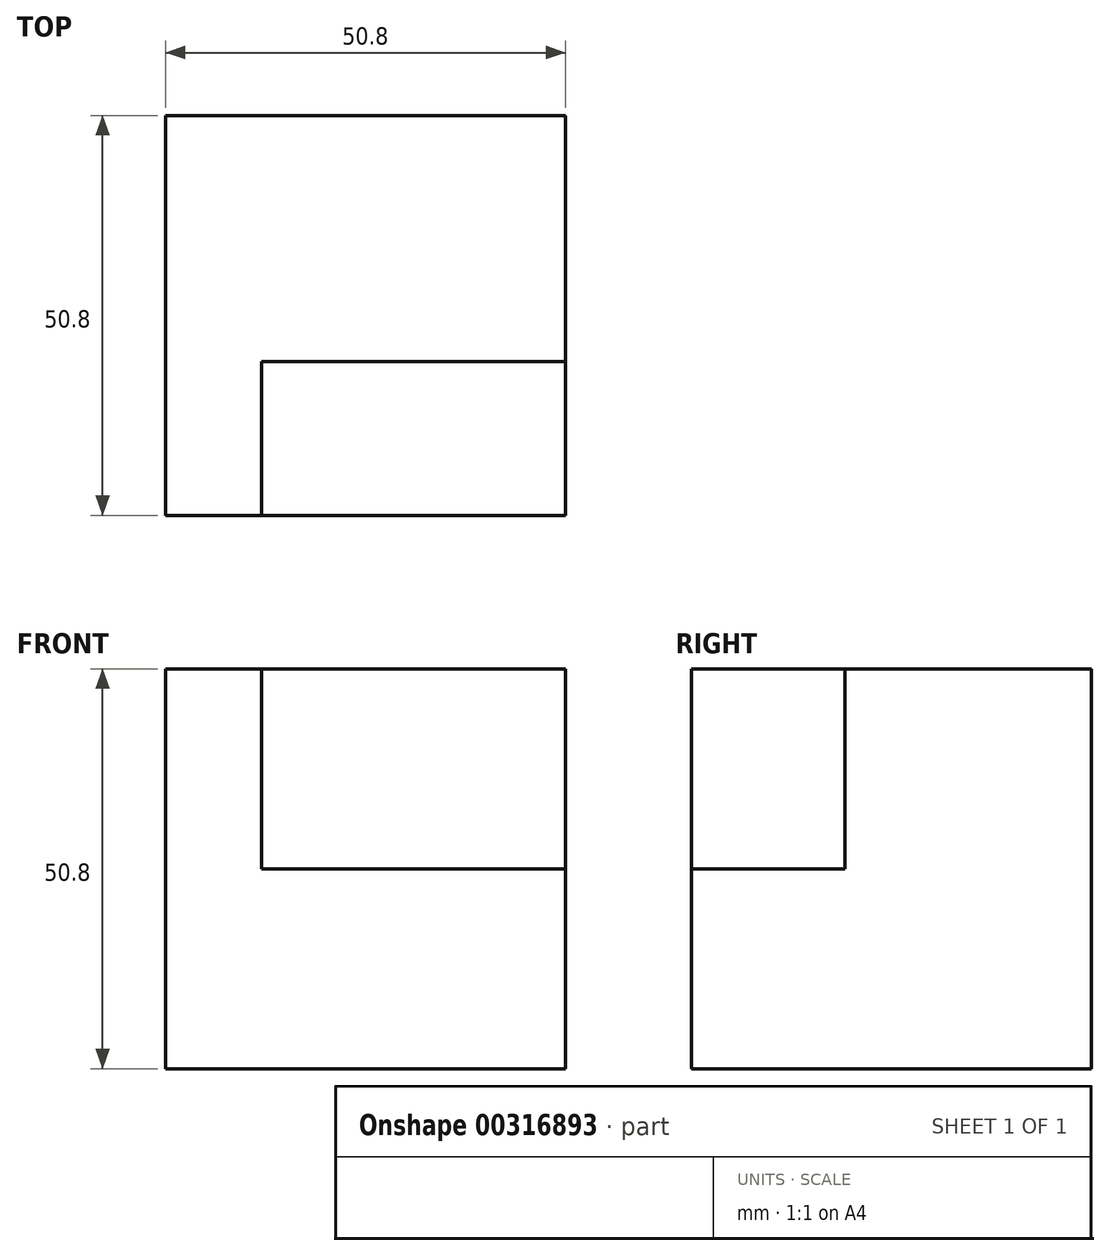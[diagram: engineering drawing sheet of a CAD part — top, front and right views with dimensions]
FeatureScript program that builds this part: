
annotation { "Feature Type Name" : "Feature", "Feature Type Description" : "" }
export const myFeature = defineFeature(function(context is Context, id is Id, definition is map)
    precondition{}
    {
        {
            var Q0;
            Q0=qCreatedBy(makeId("Top.planeOp"),FACE);
            var sketch = newSketch(context, id + "F0", { "sketchPlane" : qUnion([Q0])});
            skLineSegment(sketch, "E0", {"start": v(9.09, 37.8) * mm, "end": v(-41.71, 37.8) * mm});
            skLineSegment(sketch, "E1", {"start": v(-41.71, 37.8) * mm, "end": v(-41.71, -13) * mm});
            skLineSegment(sketch, "E2", {"start": v(-41.71, -13) * mm, "end": v(9.09, -13) * mm});
            skLineSegment(sketch, "E3", {"start": v(9.09, -13) * mm, "end": v(9.09, 37.8) * mm});
            skSolve(sketch);
        }
        {
            var Q0;
            Q0 = qSketchRegion(id + "F0", true);
            extrude(context, id + "F1", {"entities" : qUnion([Q0]), "depth" : 50.8 * mm});
        }
        {
            var Q0;
            Q0=makeQuery(id+"F1.opExtrude","CAP_FACE",FACE,{"disambiguationData":[OSD([sQuery(id+"F0.wireOp",EDGE,"E0"),sQuery(id+"F0.wireOp",EDGE,"E1"),sQuery(id+"F0.wireOp",EDGE,"E2"),sQuery(id+"F0.wireOp",EDGE,"E3")])],"isStart":false});
            var sketch = newSketch(context, id + "F2", { "sketchPlane" : qUnion([Q0])});
            skLineSegment(sketch, "E4", {"start": v(-29.5, -13) * mm, "end": v(-29.5, 6.53) * mm});
            skLineSegment(sketch, "E5", {"start": v(-29.5, 6.53) * mm, "end": v(9.09, 6.53) * mm});
            skLineSegment(sketch, "E6", {"start": v(9.09, 6.53) * mm, "end": v(9.09, -13) * mm});
            skLineSegment(sketch, "E7", {"start": v(9.09, -13) * mm, "end": v(-29.5, -13) * mm});
            skSolve(sketch);
        }
        {
            var Q0;
            Q0=makeQuery(id+"F2.imprint","IMPRINT",FACE,{"disambiguationData":[TD([[makeQuery(id+"F2.imprint","IMPRINT",EDGE,{"derivedFrom":sQuery(id+"F2.wireOp",EDGE,"E4")}),-1.0]])]});
            extrude(context, id + "F3", {"entities" : qUnion([Q0]), "operationType" : NewBodyOperationType.REMOVE, "oppositeDirection" : true, "depth" : 25.4 * mm});
        }
    });
